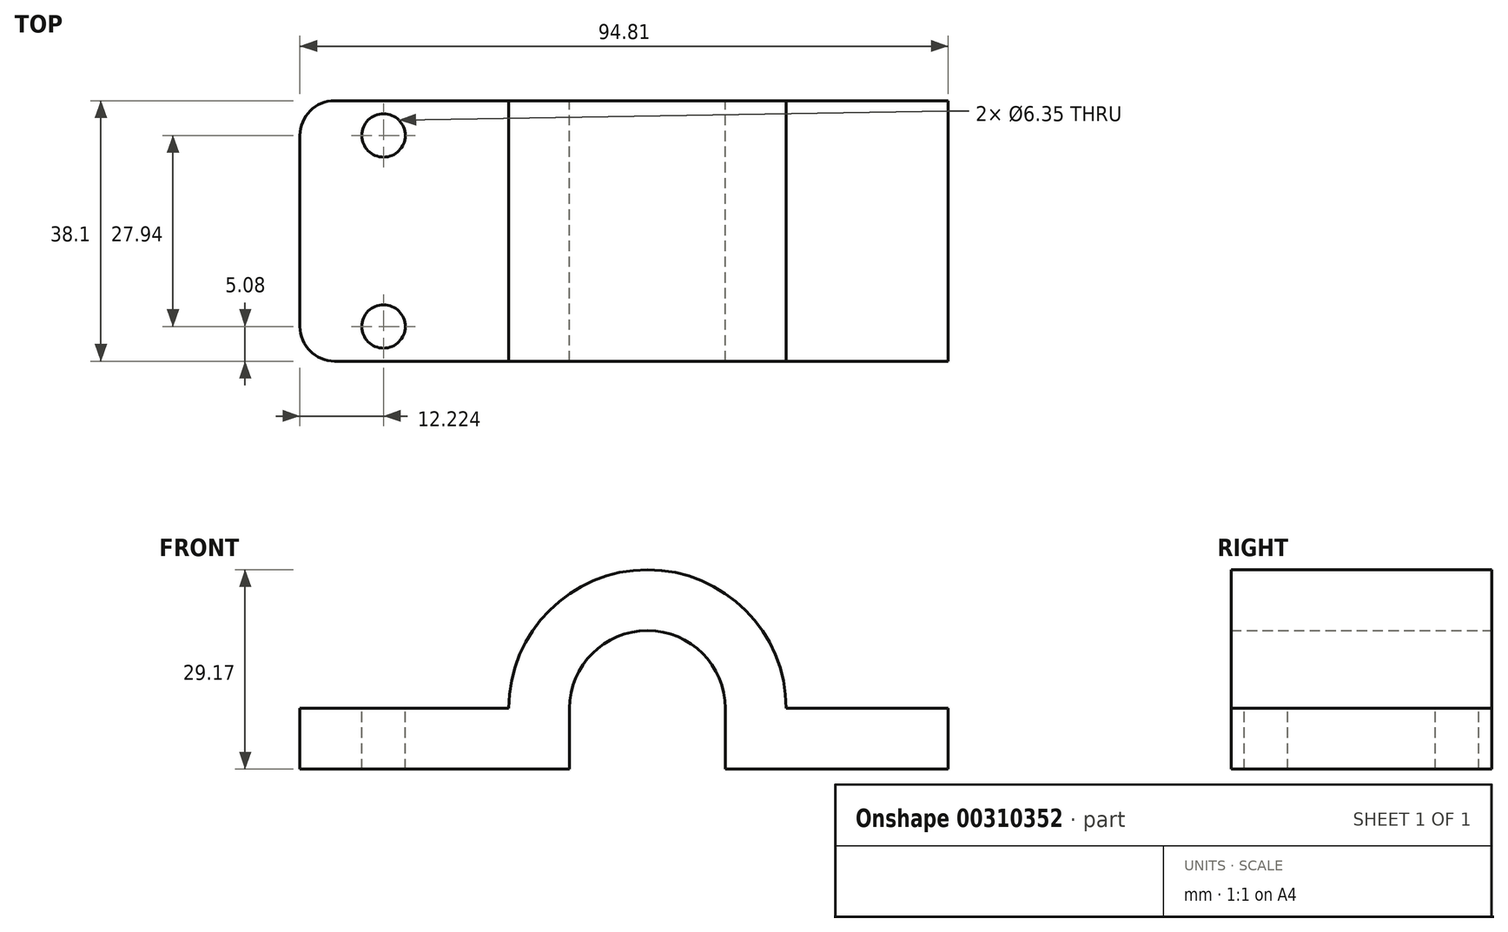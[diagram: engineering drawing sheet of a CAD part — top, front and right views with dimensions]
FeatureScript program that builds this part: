
annotation { "Feature Type Name" : "Feature", "Feature Type Description" : "" }
export const myFeature = defineFeature(function(context is Context, id is Id, definition is map)
    precondition{}
    {
        {
            var Q0;
            Q0=qCreatedBy(makeId("Front.planeOp"),FACE);
            var sketch = newSketch(context, id + "F0", { "sketchPlane" : qUnion([Q0])});
            skLineSegment(sketch, "E0.bottom", {"start": v(-31.11, 2.04) * mm, "end": v(-70.55, 2.04) * mm});
            skLineSegment(sketch, "E0.top", {"start": v(-31.11, 10.93) * mm, "end": v(-70.55, 10.93) * mm});
            skLineSegment(sketch, "E0.left", {"start": v(-31.11, 2.04) * mm, "end": v(-31.11, 10.93) * mm});
            skLineSegment(sketch, "E0.right", {"start": v(-70.55, 2.04) * mm, "end": v(-70.55, 10.93) * mm});
            skPoint(sketch, "E0.middle", {"position": v(-50.83, 6.48) * mm});
            skLineSegment(sketch, "E1.bottom", {"start": v(-8.33, 2.04) * mm, "end": v(24.26, 2.04) * mm});
            skLineSegment(sketch, "E1.top", {"start": v(-8.33, 10.93) * mm, "end": v(24.26, 10.93) * mm});
            skLineSegment(sketch, "E1.left", {"start": v(-8.33, 2.04) * mm, "end": v(-8.33, 10.93) * mm});
            skLineSegment(sketch, "E1.right", {"start": v(24.26, 2.04) * mm, "end": v(24.26, 10.93) * mm});
            skPoint(sketch, "E1.middle", {"position": v(7.96, 6.48) * mm});
            skPoint(sketch, "E1.middle.positionSnap0", {"position": v(-31.11, 6.48) * mm});
            skPoint(sketch, "E1.centerSnap0", {"position": v(-31.11, 6.48) * mm});
            skLineSegment(sketch, "E2.bottom", {"start": v(24.26, 10.93) * mm, "end": v(15.37, 10.93) * mm});
            skLineSegment(sketch, "E2.top", {"start": v(24.26, 36.55) * mm, "end": v(15.37, 36.55) * mm});
            skLineSegment(sketch, "E2.left", {"start": v(24.26, 10.93) * mm, "end": v(24.26, 36.55) * mm});
            skLineSegment(sketch, "E2.right", {"start": v(15.37, 10.93) * mm, "end": v(15.37, 36.55) * mm});
            skArc(sketch, "E3", {"start": v(-8.33, 10.93) * mm, "mid": v(-19.72, 22.32) * mm, "end": v(-31.11, 10.93) * mm});
            skArc(sketch, "E4.0", {"start": v(0.56, 10.93) * mm, "mid": v(-19.72, 31.2) * mm, "end": v(-40, 10.93) * mm});
            skSolve(sketch);
        }
        {
            var Q0;
            Q0=makeQuery(id+"F0.imprint","IMPRINT",FACE,{"disambiguationData":[TD([[makeQuery(id+"F0.imprint","IMPRINT",EDGE,{"derivedFrom":sQuery(id+"F0.wireOp",EDGE,"E0.bottom")}),-1.0]])]});
            var Q1;
            Q1=makeQuery(id+"F0.imprint","IMPRINT",FACE,{"disambiguationData":[TD([[makeQuery(id+"F0.imprint","IMPRINT",EDGE,{"derivedFrom":sQuery(id+"F0.wireOp",EDGE,"E1.bottom")}),1.0]])]});
            var Q2;
            {var subQ0=sQuery(id+"F0.wireOp",EDGE,"E3");Q2=makeQuery(id+"F0.imprint","IMPRINT",FACE,{"disambiguationData":[TD([[makeQuery(id+"F0.imprint","IMPRINT",EDGE,{"derivedFrom":subQ0}),-1.0]])]});}
            var Q3;
            Q3=makeQuery(id+"F0.imprint","IMPRINT",FACE,{"disambiguationData":[TD([[makeQuery(id+"F0.imprint","IMPRINT",EDGE,{"derivedFrom":sQuery(id+"F0.wireOp",EDGE,"E2.bottom")}),-1.0]])]});
            extrude(context, id + "F1", {"entities" : qUnion([Q0, Q1, Q2, Q3]), "endBound" : BoundingType.SYMMETRIC, "depth" : 38.1 * mm});
        }
        {
            var Q0;
            Q0=makeQuery(id+"F1.opExtrude","CAP_EDGE",EDGE,{"disambiguationData":[OSD([sQuery(id+"F0.wireOp",EDGE,"E0.right")])],"isStart":false});
            var Q1;
            Q1=makeQuery(id+"F1.opExtrude","CAP_EDGE",EDGE,{"disambiguationData":[OSD([sQuery(id+"F0.wireOp",EDGE,"E0.right")])],"isStart":true});
            var Q2;
            Q2=makeQuery(id+"F1.opExtrude","CAP_EDGE",EDGE,{"disambiguationData":[OSD([sQuery(id+"F0.wireOp",EDGE,"E2.top")])],"isStart":false});
            var Q3;
            Q3=makeQuery(id+"F1.opExtrude","CAP_EDGE",EDGE,{"disambiguationData":[OSD([sQuery(id+"F0.wireOp",EDGE,"E2.top")])],"isStart":true});
            fillet(context, id + "F2", {"entities" : qUnion([Q0, Q1, Q2, Q3]), "radius" : 5.08 * mm, "tangentPropagation" : true, "allowEdgeOverflow" : false});
        }
        {
            var Q0;
            Q0=makeQuery(id+"F1.opExtrude","SWEPT_FACE",FACE,{"disambiguationData":[OSD([sQuery(id+"F0.wireOp",EDGE,"E0.top")])]});
            var sketch = newSketch(context, id + "F3", { "sketchPlane" : qUnion([Q0])});
            skCircle(sketch, "E5", {"center": v(-58.33, 13.97) * mm, "radius": 3.25 * mm});
            skCircle(sketch, "E6", {"center": v(-58.33, -13.97) * mm, "radius": 3.22 * mm});
            skSolve(sketch);
        }
        {
            var Q0;
            Q0=sQuery(id+"F3.wireOp",VERTEX,"E5.center");
            var Q1;
            Q1=sQuery(id+"F3.wireOp",VERTEX,"E6.center");
            var Q2;
            Q2=makeQuery(id+"F1.opExtrude","SWEPT_BODY",BODY,{"disambiguationData":[OSD([sQuery(id+"F0.wireOp",EDGE,"E0.bottom"),sQuery(id+"F0.wireOp",EDGE,"E0.top"),sQuery(id+"F0.wireOp",EDGE,"E0.left"),sQuery(id+"F0.wireOp",EDGE,"E0.right"),sQuery(id+"F0.wireOp",EDGE,"E1.bottom"),sQuery(id+"F0.wireOp",EDGE,"E1.top"),sQuery(id+"F0.wireOp",EDGE,"E1.left"),sQuery(id+"F0.wireOp",EDGE,"E1.right"),sQuery(id+"F0.wireOp",EDGE,"E2.top"),sQuery(id+"F0.wireOp",EDGE,"E2.left"),sQuery(id+"F0.wireOp",EDGE,"E2.right"),sQuery(id+"F0.wireOp",EDGE,"E3"),sQuery(id+"F0.wireOp",EDGE,"E4.0")])]});
            hole(context, id + "F4", {"style" : HoleStyle.SIMPLE, "endStyle" : HoleEndStyle.THROUGH, "holeDiameter" : 6.35 * mm, "tappedDepth" : 12.7 * mm, "tapClearance" : 3, "locations" : qUnion([Q0, Q1]), "scope" : qUnion([Q2])});
        }
    });
